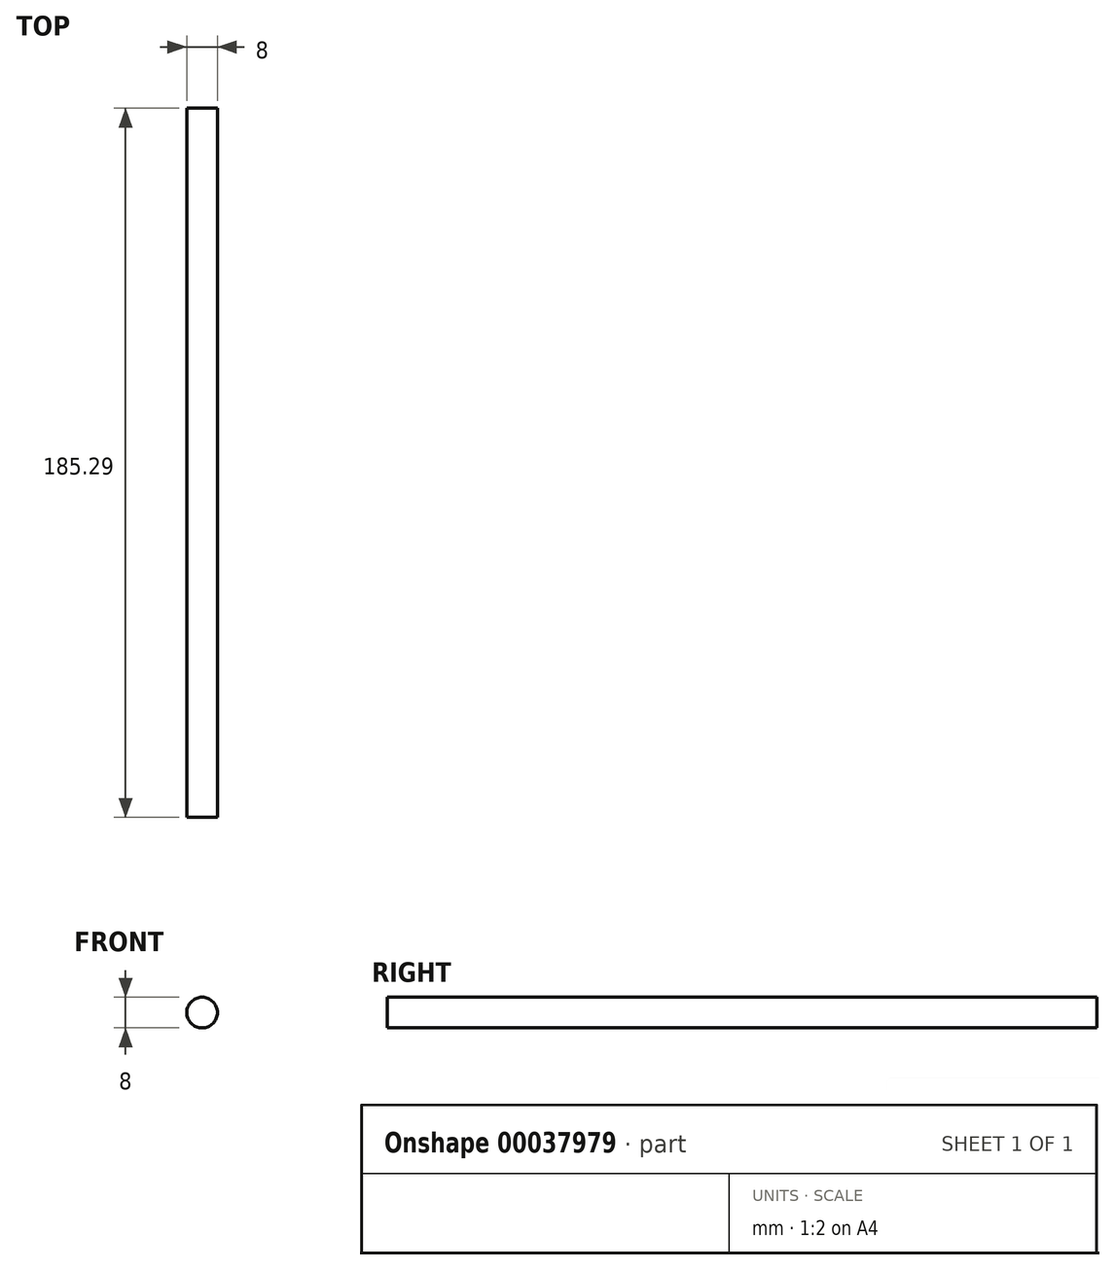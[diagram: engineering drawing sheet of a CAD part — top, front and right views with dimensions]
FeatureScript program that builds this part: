
annotation { "Feature Type Name" : "Feature", "Feature Type Description" : "" }
export const myFeature = defineFeature(function(context is Context, id is Id, definition is map)
    precondition{}
    {
        {
            var Q0;
            Q0=qCreatedBy(makeId("Front.planeOp"),FACE);
            var sketch = newSketch(context, id + "F0", { "sketchPlane" : qUnion([Q0])});
            skCircle(sketch, "E0", {"center": v(0, 0) * mm, "radius": 4 * mm});
            skSolve(sketch);
        }
        {
            var Q0;
            Q0=qSketchRegion(id+"F0",true);
            extrude(context, id + "F1", {"entities" : qUnion([Q0]), "depth" : 185.29 * mm});
        }
    });
